# Revit family: Standard-Nail-On-OXXO-Sliding-Door-with-Water-Leg-Sill-and-Standard-Hardware
name_source: partatom
category: Doors
units: mm (PartAtom-declared; Revit-internal decimal feet)

## family parameters
Always vertical = Yes
Classification Number = 23.30.10.14.11
Cut with Voids When Loaded = No
Host = Wall
Room Calculation Point = No
Shared = No

## types (1)
- 4 Panel Sliding Door - OXXO
    Analytic Construction = <None>
    Assembly Code = B2030110
    CD_Finish = Metal-Aluminum-All_Weather-Standard-White
    CD_Finish Exterior Trim = Wood-By_Others
    CD_Finish Glass = Glass-All_Weather-OA-Insulated_Glass
    CD_Finish Interior Trim = Metal-Aluminum-All_Weather-Standard-White
    CD_Finish Jamb Ext = Wood-By_Others
    CD_Head Height = 0' - 1 9/16"
    CD_Height = 8' - 0"
    CD_Height Max Panel = 12' - 0"
    CD_Height Min Panel = 3' - 10"
    CD_Height Panel = 7' - 10 3/16"
    CD_Inset = 0' - 0"
    CD_Jamb Extension = No
    CD_Jamb Width Left = 0' - 1 1/8"
    CD_Jamb Width Right = 0' - 1 1/8"
    CD_Microsite = https://microsite.caddetails.com
    CD_Number of Panels = 4
    CD_Offset = 0' - 0"
    CD_Product Documentation Link = https://www.allweatheraa.com
    CD_Product Name = Series 8150
    CD_Product Page URL = https://www.allweatheraa.com
    CD_Requested Height = 8' - 0"
    CD_Requested Width = 12' - 0"
    CD_Sill Height = 0' - 1 7/8"
    CD_Specification = http://allweatheraa.com
    CD_Thickness = 0' - 4"
    CD_Warranty = https://www.allweatheraa.com
    CD_Width = 12' - 0"
    CD_Width Max = 32' - 0 3/4"
    CD_Width Max Panel = 8' - 0"
    CD_Width Min = 10' - 8 3/4"
    CD_Width Min Panel = 2' - 8"
    CD_Width Opening = 11' - 11 1/4"
    CD_Width Panel = 3' - 1 3/32"
    CD_Width Water Sill Cover = 2' - 10 9/16"
    Center Panel Location = 1' - 5 7/32"
    Description = Thermally Broken Stacking Door
    Exterior Trim = No
    Frame Projection Ext. = 0' - 1"
    Frame Projection Int. = 0' - 1"
    Frame Width = 0' - 3"
    Function = Exterior
    Height = 8' - 0"
    Interior Trim = No
    Manufacturer = All Weather Architectural Aluminum
    Model = OXXO Water Leg Sill
    Operation = Sliding
    Rough Height = 8' - 0 1/2"
    Rough Width = 12' - 1"
    Thickness = 0' - 4"
    Type Comments = Multi-Panel Sliding Door
    URL = https://www.allweatheraa.com
    Wall Closure = By host
    Width = 12' - 0"

## geometry (parser evidence)
native form markers: Sweep x5
no freeform markers — native parametric forms only
